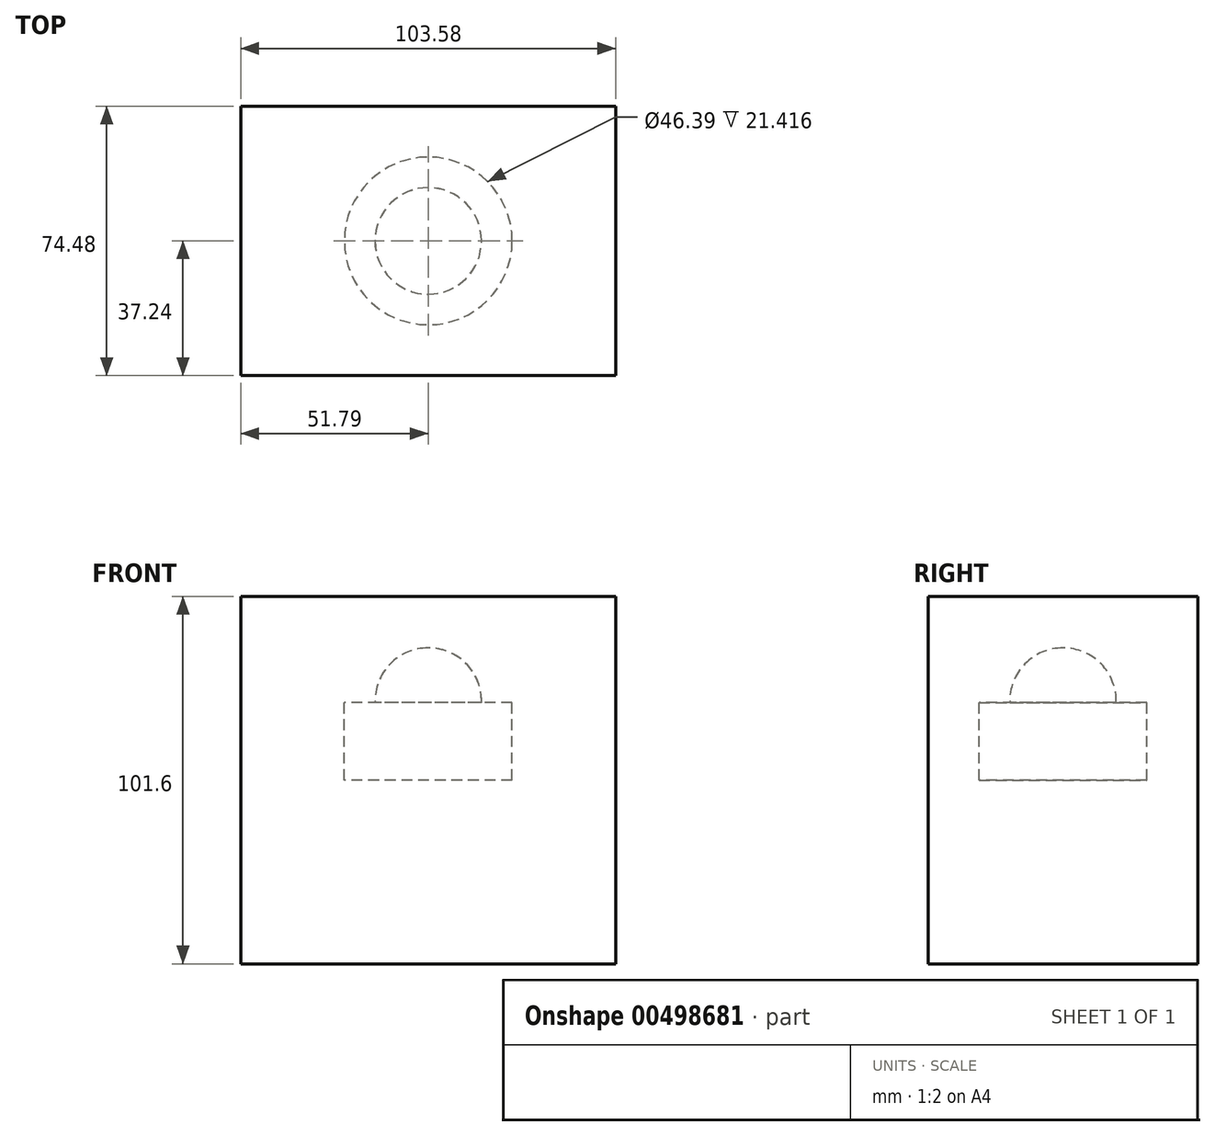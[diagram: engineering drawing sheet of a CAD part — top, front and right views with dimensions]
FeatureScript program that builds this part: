
annotation { "Feature Type Name" : "Feature", "Feature Type Description" : "" }
export const myFeature = defineFeature(function(context is Context, id is Id, definition is map)
    precondition{}
    {
        {
            var Q0;
            Q0=qCreatedBy(makeId("Top.planeOp"),FACE);
            var sketch = newSketch(context, id + "F0", { "sketchPlane" : qUnion([Q0])});
            skLineSegment(sketch, "E0.bottom", {"start": v(51.79, -37.24) * mm, "end": v(-51.79, -37.24) * mm});
            skLineSegment(sketch, "E0.top", {"start": v(51.79, 37.24) * mm, "end": v(-51.79, 37.24) * mm});
            skLineSegment(sketch, "E0.left", {"start": v(51.79, -37.24) * mm, "end": v(51.79, 37.24) * mm});
            skLineSegment(sketch, "E0.right", {"start": v(-51.79, -37.24) * mm, "end": v(-51.79, 37.24) * mm});
            skPoint(sketch, "E0.middle", {"position": v(0, 0) * mm});
            skSolve(sketch);
        }
        {
            var Q0;
            Q0=makeQuery(id+"F0.imprint","IMPRINT",FACE,{"disambiguationData":[TD([[makeQuery(id+"F0.imprint","IMPRINT",EDGE,{"derivedFrom":sQuery(id+"F0.wireOp",EDGE,"E0.bottom")}),-1.0]])]});
            extrude(context, id + "F1", {"entities" : qUnion([Q0]), "endBound" : BoundingType.SYMMETRIC, "depth" : 101.6 * mm});
        }
        {
            var Q0;
            Q0=qCreatedBy(makeId("Front.planeOp"),FACE);
            var sketch = newSketch(context, id + "F2", { "sketchPlane" : qUnion([Q0])});
            skLineSegment(sketch, "E1.bottom", {"start": v(0, 0) * mm, "end": v(23.2, 0) * mm});
            skLineSegment(sketch, "E1.left", {"start": v(0, 0) * mm, "end": v(0, 36.53) * mm});
            skLineSegment(sketch, "E1.right", {"start": v(23.2, 0) * mm, "end": v(23.2, 21.42) * mm});
            skArc(sketch, "E2", {"start": v(0, 36.53) * mm, "mid": v(10.55, 32.08) * mm, "end": v(14.72, 21.42) * mm});
            skLineSegment(sketch, "E3", {"start": v(14.72, 21.42) * mm, "end": v(23.2, 21.42) * mm});
            skSolve(sketch);
        }
        {
            var Q0;
            Q0 = qSketchRegion(id + "F2", true);
            var Q1;
            Q1=sQuery(id+"F2.wireOp",EDGE,"E3");
            var Q2;
            Q2=sQuery(id+"F2.wireOp",EDGE,"E1.left");
            revolve(context, id + "F3", {"operationType" : NewBodyOperationType.REMOVE, "entities" : qUnion([Q0]), "surfaceEntities" : qUnion([Q1]), "axis" : qUnion([Q2]), "revolveType" : RevolveType.FULL, "oppositeDirection" : true});
        }
    });
